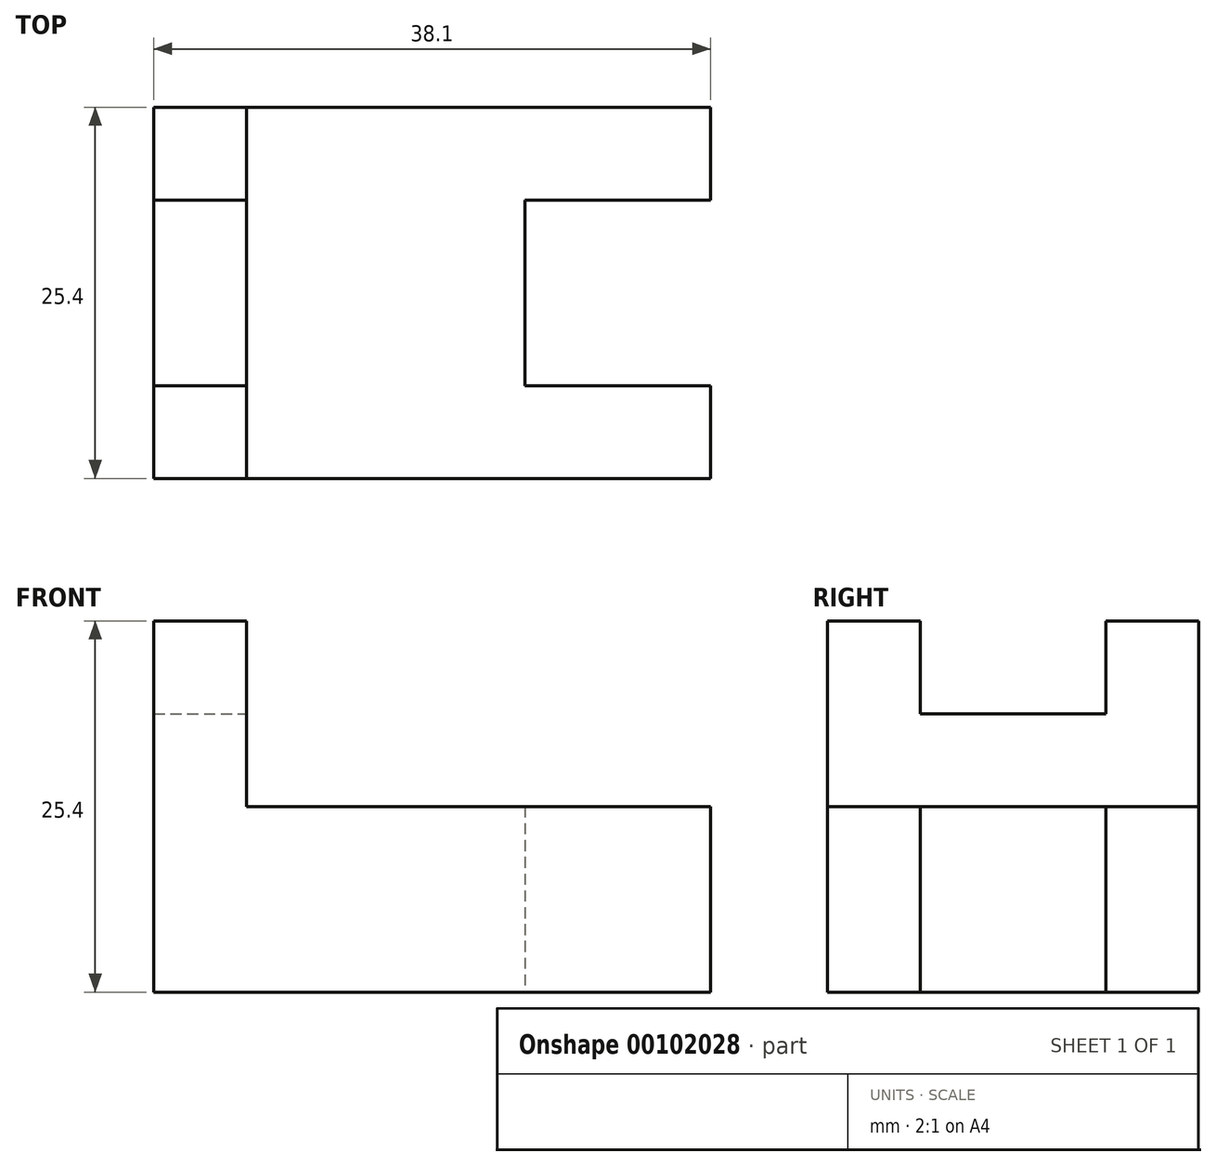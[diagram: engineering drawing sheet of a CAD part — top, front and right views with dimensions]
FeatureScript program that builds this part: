
annotation { "Feature Type Name" : "Feature", "Feature Type Description" : "" }
export const myFeature = defineFeature(function(context is Context, id is Id, definition is map)
    precondition{}
    {
        {
            var Q0;
            Q0=qCreatedBy(makeId("Front.planeOp"),FACE);
            var sketch = newSketch(context, id + "F0", { "sketchPlane" : qUnion([Q0])});
            skLineSegment(sketch, "E0", {"start": v(0, 25.4) * mm, "end": v(0, 0) * mm});
            skLineSegment(sketch, "E1", {"start": v(0, 0) * mm, "end": v(38.1, 0) * mm});
            skLineSegment(sketch, "E2", {"start": v(38.1, 0) * mm, "end": v(38.1, 12.7) * mm});
            skLineSegment(sketch, "E3", {"start": v(38.1, 12.7) * mm, "end": v(6.35, 12.7) * mm});
            skLineSegment(sketch, "E4", {"start": v(6.35, 12.7) * mm, "end": v(6.35, 25.4) * mm});
            skLineSegment(sketch, "E5", {"start": v(6.35, 25.4) * mm, "end": v(0, 25.4) * mm});
            skSolve(sketch);
        }
        {
            var Q0;
            Q0 = qSketchRegion(id + "F0", true);
            extrude(context, id + "F1", {"entities" : qUnion([Q0]), "oppositeDirection" : true, "depth" : 25.4 * mm});
        }
        {
            var Q0;
            Q0=qCreatedBy(makeId("Front.planeOp"),FACE);
            var sketch = newSketch(context, id + "F2", { "sketchPlane" : qUnion([Q0])});
            skLineSegment(sketch, "E6", {"start": v(0, 25.4) * mm, "end": v(0, 19.05) * mm});
            skLineSegment(sketch, "E7", {"start": v(0, 19.05) * mm, "end": v(6.35, 19.05) * mm});
            skLineSegment(sketch, "E8", {"start": v(6.35, 19.05) * mm, "end": v(6.35, 25.4) * mm});
            skLineSegment(sketch, "E9", {"start": v(6.35, 25.4) * mm, "end": v(0, 25.4) * mm});
            skLineSegment(sketch, "E10", {"start": v(25.4, 0) * mm, "end": v(38.1, 0) * mm});
            skLineSegment(sketch, "E11", {"start": v(38.1, 0) * mm, "end": v(38.1, 12.7) * mm});
            skLineSegment(sketch, "E12", {"start": v(38.1, 12.7) * mm, "end": v(25.4, 12.7) * mm});
            skLineSegment(sketch, "E13", {"start": v(25.4, 12.7) * mm, "end": v(25.4, 0) * mm});
            skSolve(sketch);
        }
        {
            var Q0;
            Q0 = qSketchRegion(id + "F2", true);
            extrude(context, id + "F3", {"entities" : qUnion([Q0]), "operationType" : NewBodyOperationType.REMOVE, "oppositeDirection" : true, "depth" : 19.05 * mm, "hasSecondDirection" : true, "secondDirectionOppositeDirection" : true, "secondDirectionDepth" : 6.35 * mm});
        }
    });
